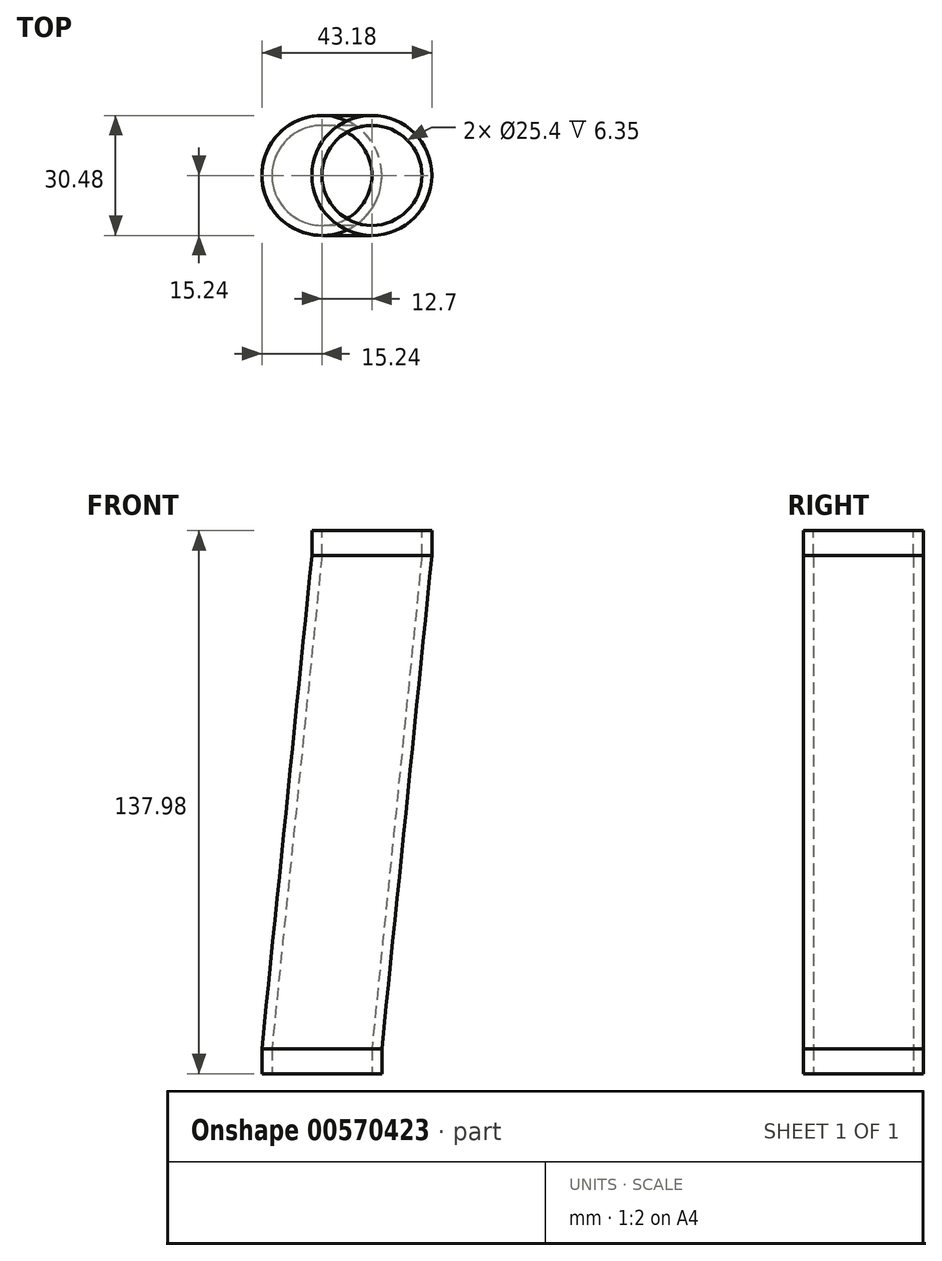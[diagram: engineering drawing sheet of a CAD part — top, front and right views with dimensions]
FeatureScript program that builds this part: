
annotation { "Feature Type Name" : "Feature", "Feature Type Description" : "" }
export const myFeature = defineFeature(function(context is Context, id is Id, definition is map)
    precondition{}
    {
        {
            var Q0;
            Q0=qCreatedBy(makeId("Top.planeOp"),FACE);
            var sketch = newSketch(context, id + "F0", { "sketchPlane" : qUnion([Q0])});
            skCircle(sketch, "E0", {"center": v(0, 0) * mm, "radius": 15.24 * mm});
            skCircle(sketch, "E1", {"center": v(0, 0) * mm, "radius": 12.7 * mm});
            skSolve(sketch);
        }
        {
            var Q0;
            Q0 = qSketchRegion(id + "F0", true);
            extrude(context, id + "F1", {"entities" : qUnion([Q0]), "depth" : 6.35 * mm, "offsetDistance" : 25.4 * mm});
        }
        {
            var Q0;
            Q0=qCreatedBy(makeId("Top.planeOp"),FACE);
            cPlane(context, id + "F2", {"entities" : qUnion([Q0]), "cplaneType" : CPlaneType.OFFSET, "offset" : 137.98 * mm, "width" : 152.4 * mm, "height" : 152.4 * mm});
        }
        {
            var Q0;
            Q0=qCreatedBy(id+"F2.planeOp",FACE);
            var sketch = newSketch(context, id + "F3", { "sketchPlane" : qUnion([Q0])});
            skLineSegment(sketch, "E2", {"start": v(0, 0) * mm, "end": v(12.7, 0) * mm, "construction": true});
            skCircle(sketch, "E3", {"center": v(12.7, 0) * mm, "radius": 15.24 * mm});
            skCircle(sketch, "E4", {"center": v(12.7, 0) * mm, "radius": 12.7 * mm});
            skSolve(sketch);
        }
        {
            var Q0;
            Q0 = qSketchRegion(id + "F3", true);
            extrude(context, id + "F4", {"entities" : qUnion([Q0]), "oppositeDirection" : true, "depth" : 6.35 * mm, "offsetDistance" : 25.4 * mm});
        }
        {
            var Q0;
            Q0=qCreatedBy(makeId("Front.planeOp"),FACE);
            var sketch = newSketch(context, id + "F5", { "sketchPlane" : qUnion([Q0])});
            skLineSegment(sketch, "E5", {"start": v(0, 0) * mm, "end": v(0, 6.35) * mm, "construction": true});
            skLineSegment(sketch, "E6", {"start": v(0, 6.35) * mm, "end": v(12.7, 131.63) * mm});
            skLineSegment(sketch, "E7", {"start": v(12.7, 131.63) * mm, "end": v(12.7, 137.98) * mm, "construction": true});
            skSolve(sketch);
        }
        {
            var Q0;
            Q0=makeQuery(id+"F1.opExtrude","CAP_FACE",FACE,{"disambiguationData":[OSD([sQuery(id+"F0.wireOp",EDGE,"E0"),sQuery(id+"F0.wireOp",EDGE,"E1")])],"isStart":false});
            var Q1;
            Q1=sQuery(id+"F5.wireOp",EDGE,"E6");
            sweep(context, id + "F6", {"profiles" : qUnion([Q0]), "path" : qUnion([Q1])});
        }
    });
